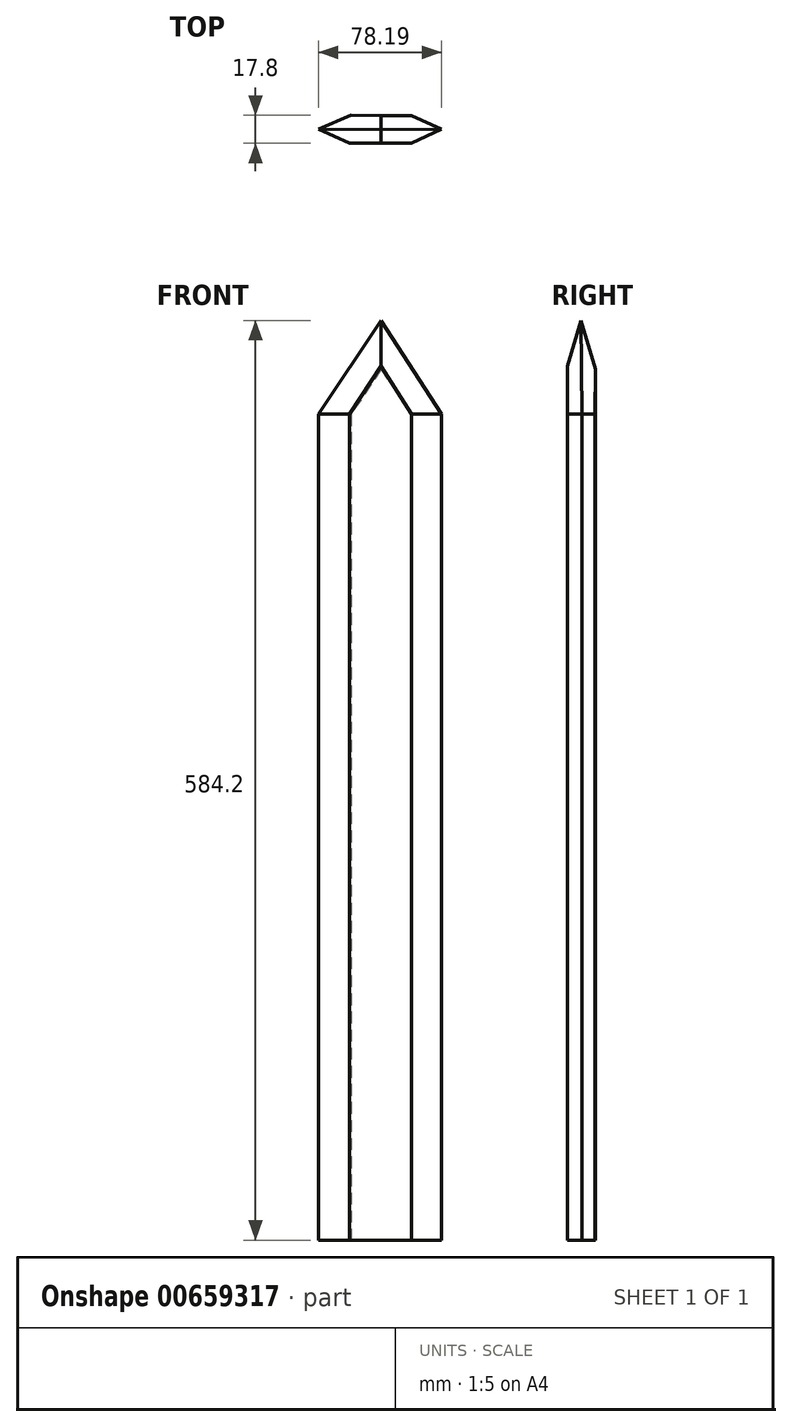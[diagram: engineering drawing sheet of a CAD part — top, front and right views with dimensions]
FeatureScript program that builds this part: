
annotation { "Feature Type Name" : "Feature", "Feature Type Description" : "" }
export const myFeature = defineFeature(function(context is Context, id is Id, definition is map)
    precondition{}
    {
        {
            var Q0;
            Q0=qCreatedBy(makeId("Top.planeOp"),FACE);
            var sketch = newSketch(context, id + "F0", { "sketchPlane" : qUnion([Q0])});
            skLineSegment(sketch, "E0.bottom", {"start": v(-40.34, -18.56) * mm, "end": v(39.23, -18.56) * mm});
            skLineSegment(sketch, "E0.top", {"start": v(-40.34, 17.67) * mm, "end": v(39.23, 17.67) * mm});
            skLineSegment(sketch, "E0.left", {"start": v(-40.34, -18.56) * mm, "end": v(-40.34, 17.67) * mm});
            skLineSegment(sketch, "E0.right", {"start": v(39.23, -18.56) * mm, "end": v(39.23, 17.67) * mm});
            skSolve(sketch);
        }
        {
            var Q0;
            Q0=makeQuery(id+"F0.imprint","IMPRINT",FACE,{"disambiguationData":[TD([[makeQuery(id+"F0.imprint","IMPRINT",EDGE,{"derivedFrom":sQuery(id+"F0.wireOp",EDGE,"E0.bottom")}),1.0]])]});
            extrude(context, id + "F1", {"entities" : qUnion([Q0]), "depth" : 12.7 * mm, "offsetDistance" : 25.4 * mm});
        }
        {
            var Q0;
            Q0=makeQuery(id+"F1.opExtrude","CAP_FACE",FACE,{"disambiguationData":[OSD([sQuery(id+"F0.wireOp",EDGE,"E0.bottom"),sQuery(id+"F0.wireOp",EDGE,"E0.top"),sQuery(id+"F0.wireOp",EDGE,"E0.left"),sQuery(id+"F0.wireOp",EDGE,"E0.right")])],"isStart":true});
            extrude(context, id + "F2", {"entities" : qUnion([Q0]), "operationType" : NewBodyOperationType.ADD, "depth" : 12.7 * mm, "offsetDistance" : 25.4 * mm});
        }
        {
            var Q0;
            Q0=makeQuery(id+"F1.opExtrude","CAP_FACE",FACE,{"disambiguationData":[OSD([sQuery(id+"F0.wireOp",EDGE,"E0.bottom"),sQuery(id+"F0.wireOp",EDGE,"E0.top"),sQuery(id+"F0.wireOp",EDGE,"E0.left"),sQuery(id+"F0.wireOp",EDGE,"E0.right")])],"isStart":false});
            var sketch = newSketch(context, id + "F3", { "sketchPlane" : qUnion([Q0])});
            skLineSegment(sketch, "E1", {"start": v(0, -17.92) * mm, "end": v(-39.6, 0) * mm});
            skLineSegment(sketch, "E2", {"start": v(0, -17.92) * mm, "end": v(38.59, 0) * mm});
            skLineSegment(sketch, "E3", {"start": v(38.59, 0) * mm, "end": v(0, 17) * mm});
            skLineSegment(sketch, "E4", {"start": v(-39.6, 0) * mm, "end": v(0, 17) * mm});
            skSolve(sketch);
        }
        {
            var Q0;
            Q0=qSketchRegion(id+"F3",true);
            extrude(context, id + "F4", {"entities" : qUnion([Q0]), "operationType" : NewBodyOperationType.ADD, "depth" : 508 * mm, "offsetDistance" : 25.4 * mm});
        }
        {
            var Q0;
            Q0=makeQuery(id+"F4.opExtrude","CAP_FACE",FACE,{"disambiguationData":[OSD([sQuery(id+"F3.wireOp",EDGE,"E1"),sQuery(id+"F3.wireOp",EDGE,"E2"),sQuery(id+"F3.wireOp",EDGE,"E3"),sQuery(id+"F3.wireOp",EDGE,"E4")])],"isStart":false});
            var sketch = newSketch(context, id + "F5", { "sketchPlane" : qUnion([Q0])});
            skSolve(sketch);
        }
        {
            var Q0;
            Q0=makeQuery(id+"F5.imprint","IMPRINT",FACE,{"disambiguationData":[TD([[makeQuery(id+"F5.imprint","IMPRINT",EDGE,{"derivedFrom":makeQuery(id+"F4.opExtrude","CAP_EDGE",EDGE,{"disambiguationData":[OSD([sQuery(id+"F3.wireOp",EDGE,"E1")])],"isStart":false})}),-1.0]])]});
            var sketch = newSketch(context, id + "F6", { "sketchPlane" : qUnion([Q0])});
            skSolve(sketch);
        }
        {
            var Q0;
            Q0=qSketchRegion(id+"F6",true);
            var Q1;
            Q1=makeQuery(id+"F5.imprint","IMPRINT",FACE,{"disambiguationData":[TD([[makeQuery(id+"F5.imprint","IMPRINT",EDGE,{"derivedFrom":makeQuery(id+"F4.opExtrude","CAP_EDGE",EDGE,{"disambiguationData":[OSD([sQuery(id+"F3.wireOp",EDGE,"E1")])],"isStart":false})}),-1.0]])]});
            extrude(context, id + "F7", {"entities" : qUnion([Q0, Q1]), "operationType" : NewBodyOperationType.ADD, "depth" : 76.2 * mm, "offsetDistance" : 25.4 * mm});
        }
        {
            var Q0;
            Q0=makeQuery(id+"F7.opExtrude","CAP_FACE",FACE,{"disambiguationData":[OSD([sQuery(id+"F3.wireOp",EDGE,"E1"),sQuery(id+"F3.wireOp",EDGE,"E2"),sQuery(id+"F3.wireOp",EDGE,"E3"),sQuery(id+"F3.wireOp",EDGE,"E4")])],"isStart":false});
            chamfer(context, id + "F8", {"entities" : qUnion([Q0]), "chamferType" : ChamferType.OFFSET_ANGLE, "width" : 59.46 * mm, "oppositeDirection" : false, "angle" : 15 * degree, "tangentPropagation" : true});
        }
        {
            var Q0;
            {var subQ0=sQuery(id+"F0.wireOp",EDGE,"E0.top");Q0=makeQuery(id+"F2.boolean.opBoolean","MERGE",FACE,{"derivedFrom":[makeQuery(id+"F1.opExtrude","SWEPT_FACE",FACE,{"disambiguationData":[OSD([subQ0])]}),makeQuery(id+"F2.opExtrude","SWEPT_FACE",FACE,{"disambiguationData":[OSD([subQ0])]})]});}
            extrude(context, id + "F9", {"entities" : qUnion([Q0]), "operationType" : NewBodyOperationType.REMOVE, "oppositeDirection" : true, "depth" : 25.4 * mm, "offsetDistance" : 25.4 * mm});
        }
        {
            var Q0;
            {var subQ0=sQuery(id+"F0.wireOp",EDGE,"E0.bottom");Q0=makeQuery(id+"F2.boolean.opBoolean","MERGE",FACE,{"derivedFrom":[makeQuery(id+"F1.opExtrude","SWEPT_FACE",FACE,{"disambiguationData":[OSD([subQ0])]}),makeQuery(id+"F2.opExtrude","SWEPT_FACE",FACE,{"disambiguationData":[OSD([subQ0])]})]});}
            extrude(context, id + "F10", {"entities" : qUnion([Q0]), "operationType" : NewBodyOperationType.REMOVE, "oppositeDirection" : true, "depth" : 25.4 * mm, "offsetDistance" : 25.4 * mm});
        }
        {
            var Q0;
            {var subQ0=sQuery(id+"F0.wireOp",EDGE,"E0.bottom");var subQ1=sQuery(id+"F0.wireOp",EDGE,"E0.top");Q0=makeQuery(id+"F10.boolean.opBoolean","MERGE",FACE,{"derivedFrom":[makeQuery(id+"F9.boolean.opBoolean","COPY",FACE,{"derivedFrom":makeQuery(id+"F9.opExtrude","SWEPT_FACE",FACE,{"disambiguationData":[OSD([subQ1]),TDD([makeQuery(id+"F1.opExtrude","CAP_EDGE",EDGE,{"disambiguationData":[OSD([subQ1])],"isStart":false})])]})}),makeQuery(id+"F10.opExtrude","SWEPT_FACE",FACE,{"disambiguationData":[OSD([subQ0]),TDD([makeQuery(id+"F1.opExtrude","CAP_EDGE",EDGE,{"disambiguationData":[OSD([subQ0])],"isStart":false})])]})]});}
            var sketch = newSketch(context, id + "F11", { "sketchPlane" : qUnion([Q0])});
            skLineSegment(sketch, "E5", {"start": v(-19.8, 8.96) * mm, "end": v(19.3, 8.96) * mm});
            skLineSegment(sketch, "E6", {"start": v(19.3, -8.5) * mm, "end": v(-19, -8.84) * mm});
            skSolve(sketch);
        }
        {
            var Q0;
            {var subQ0=sQuery(id+"F11.wireOp",EDGE,"E6");Q0=makeQuery(id+"F11.imprint","IMPRINT",FACE,{"disambiguationData":[TD([[makeQuery(id+"F11.imprint","IMPRINT",EDGE,{"derivedFrom":subQ0}),1.0]])]});}
            var Q1;
            {var subQ0=sQuery(id+"F11.wireOp",EDGE,"E5");Q1=makeQuery(id+"F11.imprint","IMPRINT",FACE,{"disambiguationData":[TD([[makeQuery(id+"F11.imprint","IMPRINT",EDGE,{"derivedFrom":subQ0}),1.0]])]});}
            extrude(context, id + "F12", {"entities" : qUnion([Q0, Q1]), "operationType" : NewBodyOperationType.REMOVE, "oppositeDirection" : true, "depth" : 990.6 * mm, "offsetDistance" : 25.4 * mm});
        }
    });
